# Revit family: Vitra_S20_Urinal_ 5461B003-0199
name_source: partatom
category: Plumbing Fixtures
revit_build: Autodesk Revit 2017 (Build: 20160225_1515(x64)
units: mm (PartAtom-declared; Revit-internal decimal feet)

## family parameters
Cut with Voids When Loaded = No
Host = Face
OmniClass Number = 23.45.05.21.11.21
OmniClass Title = Urinals
Part Type = Normal
Room Calculation Point = No
Round Connector Dimension = Use Diameter
Shared = Yes

## types (2) — shared parameters
BIMobject category = Urinals
CW Connection = Yes
Color = White
Default Elevation = 650 mm  [stored 2.13255 ft]
Description = VitrA S20
Design country = Turkey
HW Connection = No
IFC Classification = Sanitary Terminal
Main Material = Ceramic
Manufacturer = Vitra
Manufacturer name = Vitra
Masterformat 2014 Code = 22 41 13.16
Masterformat 2014 Description = Residential Urinals
MountingType = Wall Mounted
NBS Referans Code = 31-93
NBS Referans Description = Urinal And Wc Fittings
Nominal Depth = 300 mm  [stored 0.984252 ft]
NominalHeight = 600 mm
NominalWidth = 300 mm  [stored 0.984252 ft]
OmniClass Code = 23-31 21 00
OmniClass Description = Urinals
Product certification = https://vitraglobal.com
Product data url = https://www.vitra.com.tr
Product family = Wall Mounted Urinal
Product group = S20
Secondary Material = Vitra-Ceramic-White
UNSPSC Code = 30181506
URL = https://www.vitra.com.tr
Uniclass 1.4 Code = L721
Uniclass 1.4 Description = Sanitary equipment
Uniclass 2.0 Code = PR-31-93
Uniclass 2.0 Description = Urinal And Wc Fittings
Uniclass 2015 Code = Pr_40_20_93
Uniclass 2015 Name = Urinal and WC fittings
Uniformat II Code = D2010
Uniformat II Description = Plumbing Fixtures
Vent Connection = No
Warranty Period (Year) = 10 Years
Waste Connection = Yes
Weight Net (kg) = 20,927
Youtube = https://www.youtube.com
zero-valued in all types: Cost

## per-type parameters (varying)
| type | Article No. (default) | Model | Product SKU | Voltage (V) |
| Urinal_Vitra_S20Series_5461B003-0199 | 5461B003-0199 | 5461B003-0199 | 5461B003-0199 |  |
| Urinal_Vitra_S20Series(Battery-operated)_5461B003-5330 | 5461B003-5330 | 5461B003-5330 | 5461B003-5330 | Battery operated |

note: [stored X ft] marks values corroborated as IEEE doubles in the binary element streams (Revit-internal decimal feet)

## geometry (parser evidence)
native form markers: Sweep x2
no freeform markers — native parametric forms only
